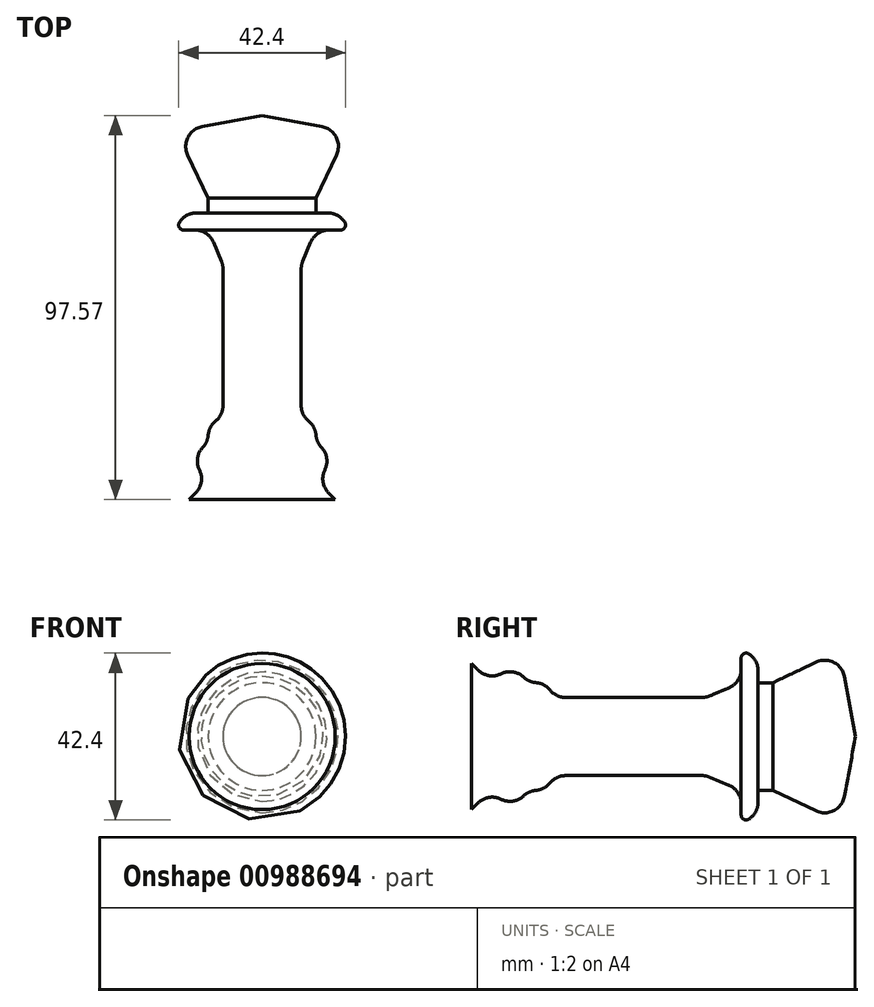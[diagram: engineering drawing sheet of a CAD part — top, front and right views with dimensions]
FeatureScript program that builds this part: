
annotation { "Feature Type Name" : "Feature", "Feature Type Description" : "" }
export const myFeature = defineFeature(function(context is Context, id is Id, definition is map)
    precondition{}
    {
        {
            var Q0;
            Q0=qCreatedBy(makeId("Top.planeOp"),FACE);
            var sketch = newSketch(context, id + "F0", { "sketchPlane" : qUnion([Q0])});
            skLineSegment(sketch, "E0", {"start": v(0, -53.1) * mm, "end": v(18.56, -53.1) * mm});
            skLineSegment(sketch, "E1", {"start": v(18.56, -53.1) * mm, "end": v(13.67, -48.2) * mm});
            skLineSegment(sketch, "E2", {"start": v(13.67, -48.2) * mm, "end": v(18.56, -43.31) * mm});
            skLineSegment(sketch, "E3", {"start": v(18.56, -43.31) * mm, "end": v(13.67, -38.42) * mm});
            skLineSegment(sketch, "E4", {"start": v(13.67, -38.42) * mm, "end": v(13.67, -34.1) * mm});
            skLineSegment(sketch, "E5", {"start": v(13.67, -34.1) * mm, "end": v(9.93, -34.1) * mm});
            skLineSegment(sketch, "E6", {"start": v(9.93, -34.1) * mm, "end": v(9.93, 6.48) * mm});
            skLineSegment(sketch, "E7", {"start": v(9.93, 6.48) * mm, "end": v(13.67, 15.4) * mm});
            skLineSegment(sketch, "E8", {"start": v(13.67, 15.4) * mm, "end": v(21.73, 15.4) * mm});
            skLineSegment(sketch, "E9", {"start": v(21.73, 15.4) * mm, "end": v(21.73, 19.71) * mm});
            skLineSegment(sketch, "E10", {"start": v(21.73, 19.71) * mm, "end": v(13.67, 19.71) * mm});
            skLineSegment(sketch, "E11", {"start": v(13.67, 19.71) * mm, "end": v(13.67, 23.46) * mm});
            skLineSegment(sketch, "E12", {"start": v(13.67, 23.46) * mm, "end": v(21.73, 40.44) * mm});
            skLineSegment(sketch, "E13", {"start": v(21.73, 40.44) * mm, "end": v(0, 44.47) * mm});
            skLineSegment(sketch, "E14", {"start": v(0, 44.47) * mm, "end": v(0, -53.1) * mm});
            skSolve(sketch);
        }
        {
            var Q0;
            Q0=makeQuery(id+"F0.imprint","IMPRINT",FACE,{"disambiguationData":[TD([[makeQuery(id+"F0.imprint","IMPRINT",EDGE,{"derivedFrom":sQuery(id+"F0.wireOp",EDGE,"E0")}),1.0]])]});
            var Q1;
            Q1=sQuery(id+"F0.wireOp",EDGE,"E14");
            revolve(context, id + "F1", {"surfaceOperationType" : NewSurfaceOperationType.NEW, "entities" : qUnion([Q0]), "axis" : qUnion([Q1]), "revolveType" : RevolveType.FULL});
        }
        {
            var Q0;
            Q0=makeQuery(id+"F1.opRevolve","SWEPT_EDGE",EDGE,{"disambiguationData":[OSD([sQuery(id+"F0.wireOp",EDGE,"E12"),sQuery(id+"F0.wireOp",EDGE,"E13")])]});
            fillet(context, id + "F2", {"entities" : qUnion([Q0]), "radius" : 5.08 * mm, "tangentPropagation" : true, "allowEdgeOverflow" : false});
        }
        {
            var Q0;
            Q0=makeQuery(id+"F1.opRevolve","SWEPT_EDGE",EDGE,{"disambiguationData":[OSD([sQuery(id+"F0.wireOp",EDGE,"E9"),sQuery(id+"F0.wireOp",EDGE,"E10")])]});
            fillet(context, id + "F3", {"entities" : qUnion([Q0]), "radius" : 5.08 * mm, "tangentPropagation" : true, "allowEdgeOverflow" : false});
        }
        {
            var Q0;
            Q0=makeQuery(id+"F1.opRevolve","SWEPT_FACE",FACE,{"disambiguationData":[OSD([sQuery(id+"F0.wireOp",EDGE,"E7")])]});
            fillet(context, id + "F4", {"entities" : qUnion([Q0]), "radius" : 5.08 * mm, "tangentPropagation" : true, "allowEdgeOverflow" : false});
        }
        {
            var Q0;
            Q0=makeQuery(id+"F1.opRevolve","SWEPT_FACE",FACE,{"disambiguationData":[OSD([sQuery(id+"F0.wireOp",EDGE,"E6")])]});
            fillet(context, id + "F5", {"entities" : qUnion([Q0]), "radius" : 5.08 * mm, "tangentPropagation" : true, "allowEdgeOverflow" : false});
        }
        {
            var Q0;
            Q0=makeQuery(id+"F1.opRevolve","SWEPT_EDGE",EDGE,{"disambiguationData":[OSD([sQuery(id+"F0.wireOp",EDGE,"E2"),sQuery(id+"F0.wireOp",EDGE,"E3")])]});
            fillet(context, id + "F6", {"entities" : qUnion([Q0]), "radius" : 5.08 * mm, "tangentPropagation" : true, "allowEdgeOverflow" : false});
        }
        {
            var Q0;
            Q0=makeQuery(id+"F1.opRevolve","SWEPT_EDGE",EDGE,{"disambiguationData":[OSD([sQuery(id+"F0.wireOp",EDGE,"E3"),sQuery(id+"F0.wireOp",EDGE,"E4")])]});
            fillet(context, id + "F7", {"entities" : qUnion([Q0]), "radius" : 5.08 * mm, "tangentPropagation" : true, "allowEdgeOverflow" : false});
        }
        {
            var Q0;
            Q0=makeQuery(id+"F1.opRevolve","SWEPT_EDGE",EDGE,{"disambiguationData":[OSD([sQuery(id+"F0.wireOp",EDGE,"E1"),sQuery(id+"F0.wireOp",EDGE,"E2")])]});
            fillet(context, id + "F8", {"entities" : qUnion([Q0]), "radius" : 5.08 * mm, "tangentPropagation" : true, "allowEdgeOverflow" : false});
        }
        {
            var Q0;
            Q0=makeQuery(id+"F3.opFillet","BLEND_EDGE",EDGE,{"blendedFrom":[makeQuery(id+"F1.opRevolve","SWEPT_EDGE",EDGE,{"disambiguationData":[OSD([sQuery(id+"F0.wireOp",EDGE,"E9"),sQuery(id+"F0.wireOp",EDGE,"E10")])]}),makeQuery(id+"F1.opRevolve","SWEPT_FACE",FACE,{"disambiguationData":[OSD([sQuery(id+"F0.wireOp",EDGE,"E8")])]})],"blendedInto":[makeQuery(id+"F1.opRevolve","SWEPT_FACE",FACE,{"disambiguationData":[OSD([sQuery(id+"F0.wireOp",EDGE,"E8")])]})]});
            fillet(context, id + "F9", {"entities" : qUnion([Q0]), "radius" : 1.27 * mm, "tangentPropagation" : true, "allowEdgeOverflow" : false});
        }
        {
            var Q0;
            Q0=makeQuery(id+"F5.opFillet","BLEND_EDGE",EDGE,{"blendedFrom":[makeQuery(id+"F1.opRevolve","SWEPT_EDGE",EDGE,{"disambiguationData":[OSD([sQuery(id+"F0.wireOp",EDGE,"E5"),sQuery(id+"F0.wireOp",EDGE,"E6")])]}),makeQuery(id+"F1.opRevolve","SWEPT_FACE",FACE,{"disambiguationData":[OSD([sQuery(id+"F0.wireOp",EDGE,"E4")])]})],"blendedInto":[makeQuery(id+"F1.opRevolve","SWEPT_FACE",FACE,{"disambiguationData":[OSD([sQuery(id+"F0.wireOp",EDGE,"E4")])]})]});
            fillet(context, id + "F10", {"entities" : qUnion([Q0]), "radius" : 5.08 * mm, "tangentPropagation" : true, "allowEdgeOverflow" : false});
        }
    });
